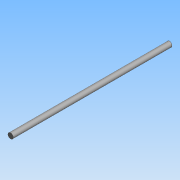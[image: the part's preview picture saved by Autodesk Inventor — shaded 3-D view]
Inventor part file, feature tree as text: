
AUTODESK INVENTOR PART (.ipt)
format: ipt  version: 2015 (Build 190159000, 159)  size: 65,024 bytes
history: native  units: mm
features: extrude x1, sketch x1
ambient origin geometry x8: Origin, YZ Plane, XZ Plane, XY Plane, X Axis, Y Axis, Z Axis, Center Point
bodies: Solid1 (feature_tree)
feature tree (2):
  extrude  "Extrusion1"  Depth=150.0mm TaperAngle=0.0deg
  sketch  "Sketch1"  dims[d0=5.0mm d1=150.0mm d2=0.0mm]
